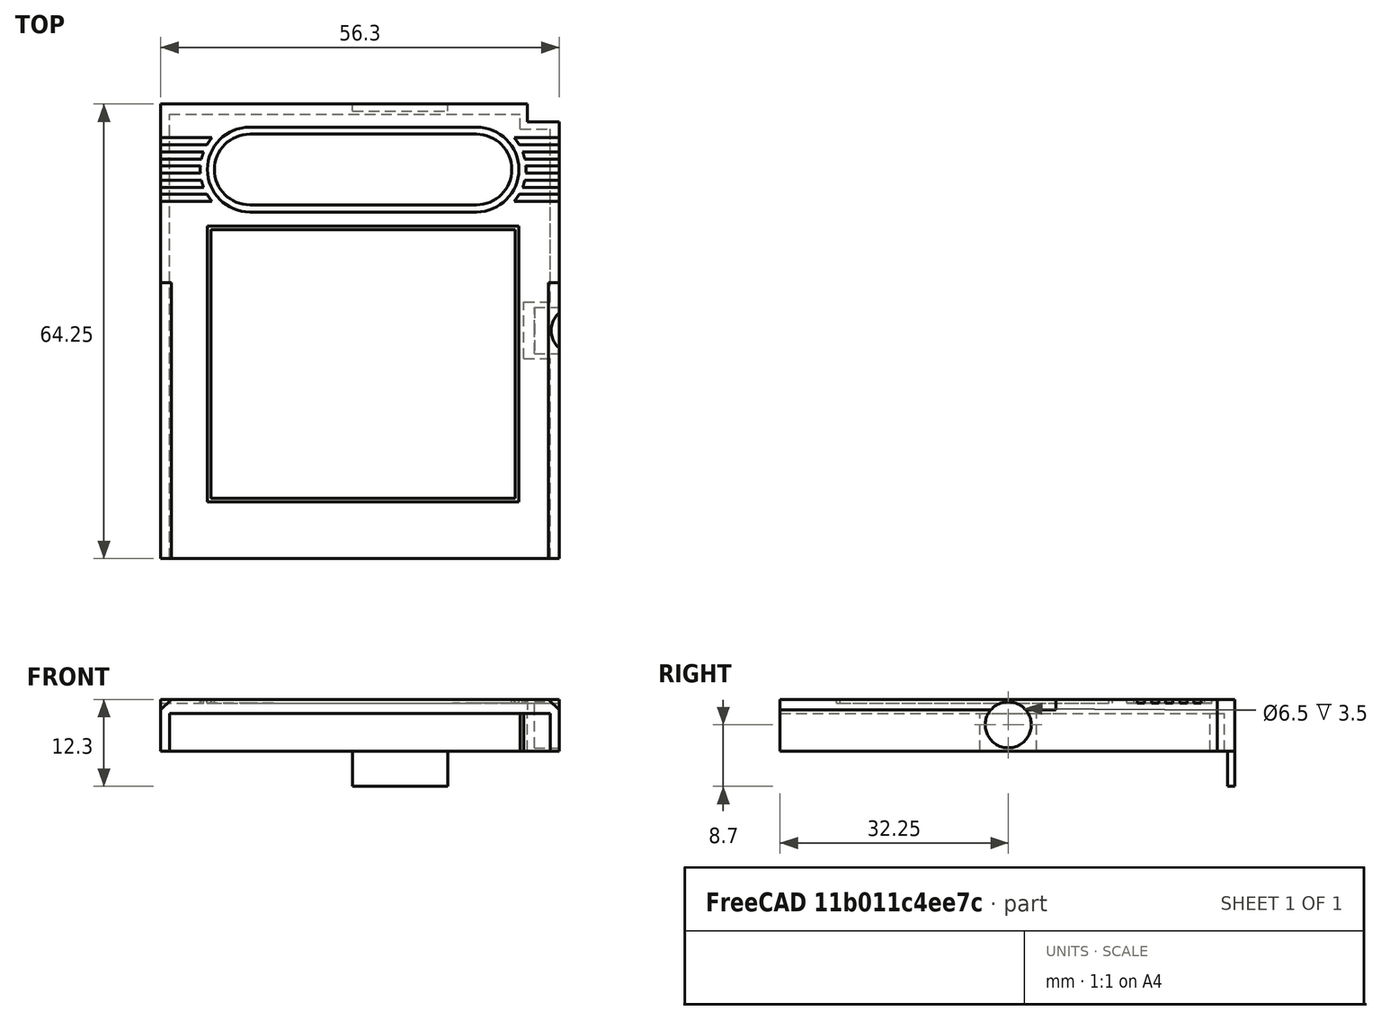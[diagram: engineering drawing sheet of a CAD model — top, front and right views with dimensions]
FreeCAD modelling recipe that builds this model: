
FCSTD DOCUMENT  (FreeCAD 0.18R16131 (Git))
Label: GBC_gameboy_cart_cover
License: All rights reserved
LicenseURL: http://en.wikipedia.org/wiki/All_rights_reserved
objects: Part::Box×23, Part::Cut×12, Part::Cylinder×7, Part::MultiFuse×6, Part::Chamfer×1
note: 49 computed .brp shape members not serialized (recipe doc carries the construction recipe); baked Part::Feature solids carry a one-line shape summary decoded from their .brp

FEATURE [Part::Box] Box  label="Cube(outer_base)"
  AttacherType = Attacher::AttachEngine3D
  Height = 5.3
  Length = 56.3
  Width = 64.25
FEATURE [Part::Box] Box001  label="Cube(corner_inner)"
  AttacherType = Attacher::AttachEngine3D
  Height = 5.3
  Length = 4.5
  Placement = pos=(51.8,61.75,0) rot=(0,0,1;0rad)
  Width = 2.5
FEATURE [Part::Box] Box002  label="Cube(inner_base)"
  AttacherType = Attacher::AttachEngine3D
  Height = 5.3
  Length = 53.8
  Placement = pos=(1.25,0,0) rot=(0,0,1;0rad)
  Width = 62.8
FEATURE [Part::Box] Box003  label="Cube(corner_outer)"
  AttacherType = Attacher::AttachEngine3D
  Height = 5.3
  Length = 5.5
  Placement = pos=(50.8,60.75,0) rot=(0,0,1;0rad)
  Width = 3.5
FEATURE [Part::Box] Box007  label="Cube(top_cover_top_half)"
  AttacherType = Attacher::AttachEngine3D
  Height = 2
  Length = 56.3
  Placement = pos=(0,39,5.3) rot=(0,0,1;0rad)
  Width = 25.25
FEATURE [Part::Box] Box008  label="Cube001(top_cover_bottom_half)"
  AttacherType = Attacher::AttachEngine3D
  Height = 2
  Length = 56.3
  Placement = pos=(0,0,5.3) rot=(0,0,1;0rad)
  Width = 39
FEATURE [Part::Chamfer] Chamfer
  Base = -> Box008
  Edges = 2 edges r=1.5: [Edge2,Edge6]
FEATURE [Part::Box] Box010  label="Cube(top_corner_cut)"
  AttacherType = Attacher::AttachEngine3D
  Height = 10
  Length = 10
  Placement = pos=(51.8,61.75,0) rot=(0,0,1;0rad)
  Width = 10
FEATURE [Part::Cut] Cut006
  Base = -> Box007
  Tool = -> Box010
FEATURE [Part::Box] Box017  label="Cube(game_lable_inner)"
  AttacherType = Attacher::AttachEngine3D
  Height = 0.5
  Length = 43
  Placement = pos=(7.1,8.5,6.8) rot=(0,0,1;0rad)
  Width = 38
FEATURE [Part::Box] Box041  label="Cube(game_lable_outer)"
  AttacherType = Attacher::AttachEngine3D
  Height = 0.5
  Length = 44
  Placement = pos=(6.6,8,6.8) rot=(0,0,1;0rad)
  Width = 39
FEATURE [Part::Cylinder] Cylinder006  label="Cylinder001(left_nintendo_outer)"
  Angle = 360
  AttacherType = Attacher::AttachEngine3D
  Height = 1
  Placement = pos=(12.6,55,6.8) rot=(0,0,1;0rad)
  Radius = 6
FEATURE [Part::Cylinder] Cylinder007  label="Cylinder002(right_nintendo_outer)"
  Angle = 360
  AttacherType = Attacher::AttachEngine3D
  Height = 1
  Placement = pos=(44.6,55,6.8) rot=(0,0,1;0rad)
  Radius = 6
FEATURE [Part::Box] Box044  label="Cube(middle_nintendo_outer)"
  AttacherType = Attacher::AttachEngine3D
  Height = 1
  Length = 32
  Placement = pos=(12.6,49,6.8) rot=(0,0,1;0rad)
  Width = 12
FEATURE [Part::Box] Box045  label="Cube(left_fin_1)"
  AttacherType = Attacher::AttachEngine3D
  Height = 1
  Length = 10
  Placement = pos=(0,50.5,6.8) rot=(0,0,1;0rad)
  Width = 1
FEATURE [Part::Box] Box046  label="Cube001(left_fin_5)"
  AttacherType = Attacher::AttachEngine3D
  Height = 1
  Length = 10
  Placement = pos=(0,52.5,6.8) rot=(0,0,1;0rad)
  Width = 1
FEATURE [Part::Box] Box047  label="Cube002(left_fin_2)"
  AttacherType = Attacher::AttachEngine3D
  Height = 1
  Length = 10
  Placement = pos=(0,54.5,6.8) rot=(0,0,1;0rad)
  Width = 1
FEATURE [Part::Box] Box048  label="Cube003(left_fin_4)"
  AttacherType = Attacher::AttachEngine3D
  Height = 1
  Length = 10
  Placement = pos=(0,56.5,6.8) rot=(0,0,1;0rad)
  Width = 1
FEATURE [Part::Box] Box049  label="Cube004(left_fin_3)"
  AttacherType = Attacher::AttachEngine3D
  Height = 1
  Length = 10
  Placement = pos=(0,58.5,6.8) rot=(0,0,1;0rad)
  Width = 1
FEATURE [Part::Cylinder] Cylinder008  label="Cylinder001(left_nintendo_fin_cut)"
  Angle = 360
  AttacherType = Attacher::AttachEngine3D
  Height = 1
  Placement = pos=(12.6,55,6.8) rot=(0,0,1;0rad)
  Radius = 7
FEATURE [Part::Box] Box050  label="Cube(right_fin_1)"
  AttacherType = Attacher::AttachEngine3D
  Height = 1
  Length = 10
  Placement = pos=(46.3,50.5,6.8) rot=(0,0,1;0rad)
  Width = 1
FEATURE [Part::Box] Box051  label="Cube002(right_fin_2)"
  AttacherType = Attacher::AttachEngine3D
  Height = 1
  Length = 10
  Placement = pos=(46.3,54.5,6.8) rot=(0,0,1;0rad)
  Width = 1
FEATURE [Part::Box] Box052  label="Cube004(right_fin_3)"
  AttacherType = Attacher::AttachEngine3D
  Height = 1
  Length = 10
  Placement = pos=(46.3,58.5,6.8) rot=(0,0,1;0rad)
  Width = 1
FEATURE [Part::Box] Box053  label="Cube003(right_fin_4)"
  AttacherType = Attacher::AttachEngine3D
  Height = 1
  Length = 10
  Placement = pos=(46.3,56.5,6.8) rot=(0,0,1;0rad)
  Width = 1
FEATURE [Part::Box] Box054  label="Cube001(right_fin_5)"
  AttacherType = Attacher::AttachEngine3D
  Height = 1
  Length = 10
  Placement = pos=(46.3,52.5,6.8) rot=(0,0,1;0rad)
  Width = 1
FEATURE [Part::Cylinder] Cylinder009  label="Cylinder002(right_nintendo_fin_cut)"
  Angle = 360
  AttacherType = Attacher::AttachEngine3D
  Height = 1
  Placement = pos=(44.6,55,6.8) rot=(0,0,1;0rad)
  Radius = 7
FEATURE [Part::MultiFuse] Fusion003
  Shapes = -> [Box050,Box051,Box054,Box053,Box052]
FEATURE [Part::Cut] Cut008
  Base = -> Fusion003
  Tool = -> Cylinder009
FEATURE [Part::MultiFuse] Fusion004
  Shapes = -> [Box045,Box047,Box049,Box048,Box046]
FEATURE [Part::Cut] Cut009
  Base = -> Fusion004
  Tool = -> Cylinder008
FEATURE [Part::Cylinder] Cylinder010  label="Cylinder001(left_nintendo_inner)"
  Angle = 360
  AttacherType = Attacher::AttachEngine3D
  Height = 0.5
  Placement = pos=(12.6,55,6.8) rot=(0,0,1;0rad)
  Radius = 5
FEATURE [Part::Cylinder] Cylinder011  label="Cylinder002(right_nintendo_inner)"
  Angle = 360
  AttacherType = Attacher::AttachEngine3D
  Height = 0.5
  Placement = pos=(44.6,55,6.8) rot=(0,0,1;0rad)
  Radius = 5
FEATURE [Part::Box] Box055  label="Cube(middle_nintendo_inner)"
  AttacherType = Attacher::AttachEngine3D
  Height = 0.5
  Length = 32
  Placement = pos=(12.6,50,6.8) rot=(0,0,1;0rad)
  Width = 10
FEATURE [Part::Cut] Cut010
  Base = -> Cut006
  Tool = -> Cut008
FEATURE [Part::Cut] Cut011
  Base = -> Cut010
  Tool = -> Cut009
FEATURE [Part::Cut] Cut012
  Base = -> Cut011
  Tool = -> Cylinder006
FEATURE [Part::Cut] Cut013
  Base = -> Cut012
  Tool = -> Cylinder007
FEATURE [Part::Cut] Cut014
  Base = -> Cut013
  Tool = -> Box044
FEATURE [Part::MultiFuse] Fusion033
  Shapes = -> [Cylinder010,Cylinder011,Box055]
FEATURE [Part::Cut] Cut
  Base = -> Box
  Tool = -> Box002
FEATURE [Part::MultiFuse] Fusion
  Shapes = -> [Cut,Box003]
FEATURE [Part::Cut] Cut024
  Base = -> Fusion
  Tool = -> Box001
FEATURE [Part::Box] Box056  label="Cube(sd_card_cover)"
  AttacherType = Attacher::AttachEngine3D
  Height = 5
  Length = 13.5
  Placement = pos=(27.1,63.25,-5) rot=(0,0,1;0rad)
  Width = 1
FEATURE [Part::Box] Box057  label="Cube(magnet_black)"
  AttacherType = Attacher::AttachEngine3D
  Height = 5.3
  Length = 4
  Placement = pos=(51.3,28.25,0) rot=(0,0,1;0rad)
  Width = 8
FEATURE [Part::Cylinder] Cylinder  label="Cylinder(magnet)"
  Angle = 360
  AttacherType = Attacher::AttachEngine3D
  Height = 3.5
  Placement = pos=(52.8,32.25,3.7) rot=(0,1,0;1.5708rad)
  Radius = 3.25
FEATURE [Part::MultiFuse] Fusion034
  Shapes = -> [Cut014,Chamfer,Fusion033]
FEATURE [Part::Cut] Cut025
  Base = -> Fusion034
  Tool = -> Box041
FEATURE [Part::MultiFuse] Fusion035
  Shapes = -> [Cut025,Box017,Box057,Cut024,Box056]
FEATURE [Part::Cut] Cut026
  Base = -> Fusion035
  Tool = -> Cylinder
